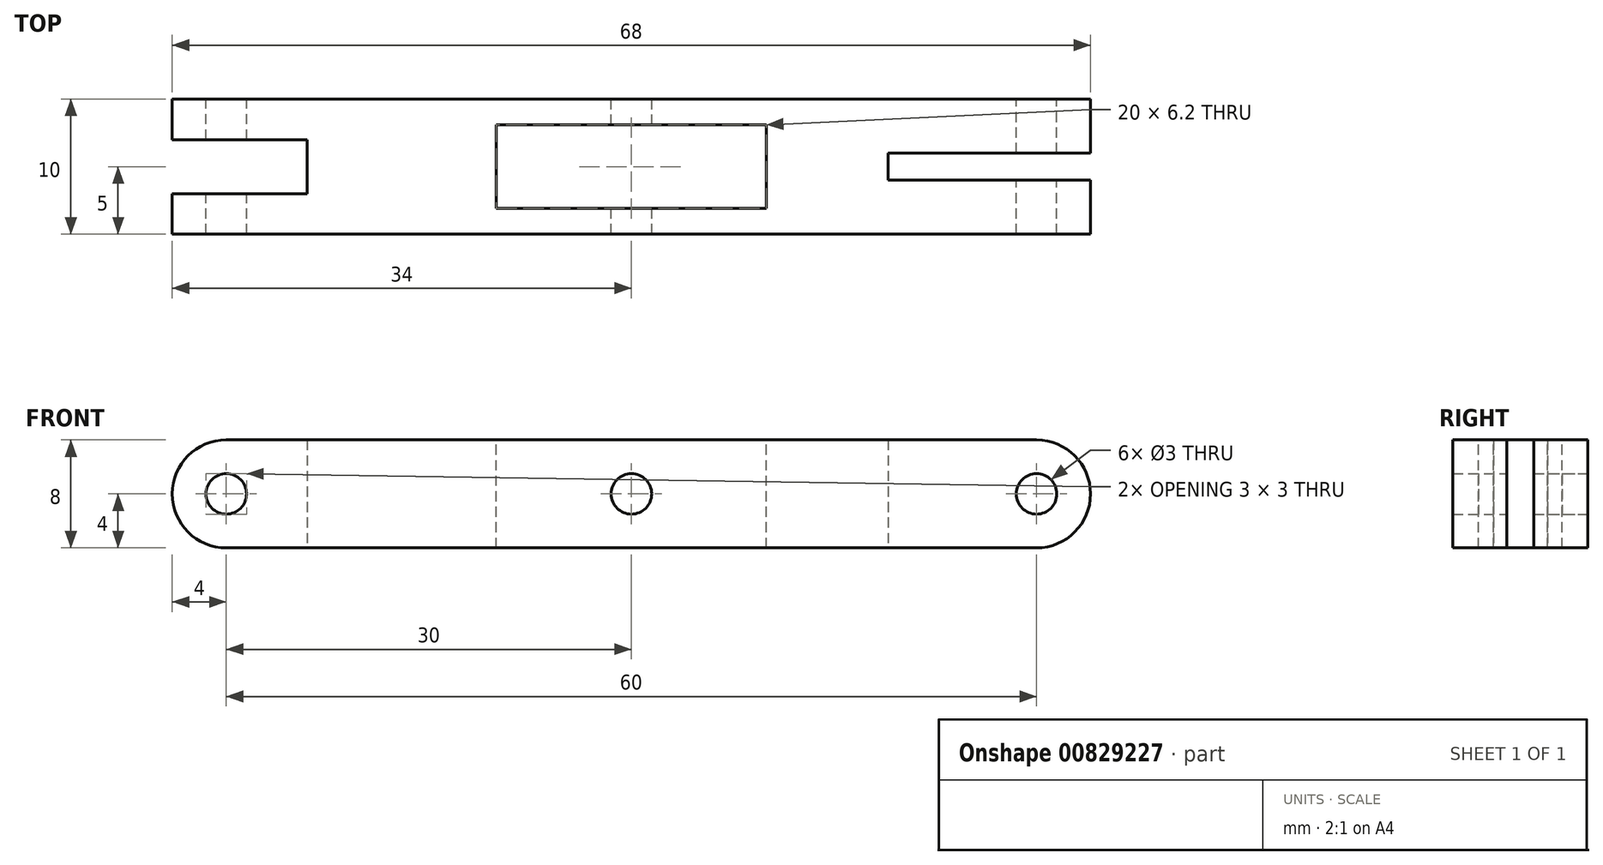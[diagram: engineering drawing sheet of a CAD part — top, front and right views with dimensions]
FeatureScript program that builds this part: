
annotation { "Feature Type Name" : "Feature", "Feature Type Description" : "" }
export const myFeature = defineFeature(function(context is Context, id is Id, definition is map)
    precondition{}
    {
        {
            var Q0;
            Q0=qCreatedBy(makeId("Front.planeOp"),FACE);
            var sketch = newSketch(context, id + "F0", { "sketchPlane" : qUnion([Q0])});
            skLineSegment(sketch, "E0.bottom", {"start": v(30, 4) * mm, "end": v(-30, 4) * mm});
            skLineSegment(sketch, "E0.top", {"start": v(30, -4) * mm, "end": v(-30, -4) * mm});
            skPoint(sketch, "E0.middle", {"position": v(0, 0) * mm});
            skArc(sketch, "E1", {"start": v(-30, 4) * mm, "mid": v(-34, 0) * mm, "end": v(-30, -4) * mm});
            skArc(sketch, "E2", {"start": v(30, -4) * mm, "mid": v(34, 0) * mm, "end": v(30, 4) * mm});
            skCircle(sketch, "E3", {"center": v(-30, 0) * mm, "radius": 1.5 * mm});
            skCircle(sketch, "E4", {"center": v(0, 0) * mm, "radius": 1.5 * mm});
            skCircle(sketch, "E5", {"center": v(30, 0) * mm, "radius": 1.5 * mm});
            skSolve(sketch);
        }
        {
            var Q0;
            Q0 = qSketchRegion(id + "F0", true);
            extrude(context, id + "F1", {"entities" : qUnion([Q0]), "endBound" : BoundingType.SYMMETRIC, "depth" : 10 * mm, "offsetDistance" : 25 * mm});
        }
        {
            var Q0;
            Q0=qCreatedBy(makeId("Right.planeOp"),FACE);
            cPlane(context, id + "F2", {"entities" : qUnion([Q0]), "cplaneType" : CPlaneType.OFFSET, "offset" : 64 * mm, "width" : 150 * mm, "height" : 150 * mm});
        }
        {
            var Q0;
            Q0=qCreatedBy(id+"F2.planeOp",FACE);
            var sketch = newSketch(context, id + "F3", { "sketchPlane" : qUnion([Q0])});
            skLineSegment(sketch, "E6.bottom", {"start": v(1, 4) * mm, "end": v(-1, 4) * mm});
            skLineSegment(sketch, "E6.top", {"start": v(1, -4) * mm, "end": v(-1, -4) * mm});
            skLineSegment(sketch, "E6.left", {"start": v(1, 4) * mm, "end": v(1, -4) * mm});
            skLineSegment(sketch, "E6.right", {"start": v(-1, 4) * mm, "end": v(-1, -4) * mm});
            skPoint(sketch, "E6.middle", {"position": v(0, 0) * mm});
            skSolve(sketch);
        }
        {
            var Q0;
            Q0=makeQuery(id+"F3.imprint","IMPRINT",FACE,{"disambiguationData":[TD([[makeQuery(id+"F3.imprint","IMPRINT",EDGE,{"derivedFrom":sQuery(id+"F3.wireOp",EDGE,"E6.bottom")}),1.0]])]});
            extrude(context, id + "F4", {"entities" : qUnion([Q0]), "operationType" : NewBodyOperationType.REMOVE, "oppositeDirection" : true, "depth" : 45 * mm, "offsetDistance" : 25 * mm});
        }
        {
            var Q0;
            Q0=makeQuery(id+"F1.opExtrude","SWEPT_FACE",FACE,{"disambiguationData":[OSD([sQuery(id+"F0.wireOp",EDGE,"E0.bottom")])]});
            var sketch = newSketch(context, id + "F5", { "sketchPlane" : qUnion([Q0])});
            skSolve(sketch);
        }
        {
            var Q0;
            {var subQ2=sQuery(id+"F0.wireOp",EDGE,"E0.bottom");Q0=makeQuery(id+"F5.imprint","IMPRINT",FACE,{"disambiguationData":[TD([[makeQuery(id+"F5.imprint","IMPRINT",EDGE,{"derivedFrom":makeQuery(id+"F1.opExtrude","CAP_EDGE",EDGE,{"disambiguationData":[OSD([subQ2])],"isStart":true})}),1.0]])]});}
            var sketch = newSketch(context, id + "F6", { "sketchPlane" : qUnion([Q0])});
            skLineSegment(sketch, "E7.bottom", {"start": v(10, 3.1) * mm, "end": v(-10, 3.1) * mm});
            skLineSegment(sketch, "E7.top", {"start": v(10, -3.1) * mm, "end": v(-10, -3.1) * mm});
            skLineSegment(sketch, "E7.left", {"start": v(10, 3.1) * mm, "end": v(10, -3.1) * mm});
            skLineSegment(sketch, "E7.right", {"start": v(-10, 3.1) * mm, "end": v(-10, -3.1) * mm});
            skPoint(sketch, "E7.middle", {"position": v(0, 0) * mm});
            skSolve(sketch);
        }
        {
            var Q0;
            Q0 = qSketchRegion(id + "F6", true);
            extrude(context, id + "F7", {"entities" : qUnion([Q0]), "operationType" : NewBodyOperationType.REMOVE, "oppositeDirection" : true, "depth" : 25 * mm, "offsetDistance" : 25 * mm});
        }
        {
            var Q0;
            Q0=qCreatedBy(makeId("Right.planeOp"),FACE);
            cPlane(context, id + "F8", {"entities" : qUnion([Q0]), "cplaneType" : CPlaneType.OFFSET, "offset" : 64 * mm, "oppositeDirection" : true, "width" : 150 * mm, "height" : 150 * mm});
        }
        {
            var Q0;
            Q0=qCreatedBy(id+"F8.planeOp",FACE);
            var sketch = newSketch(context, id + "F9", { "sketchPlane" : qUnion([Q0])});
            skLineSegment(sketch, "E8.bottom", {"start": v(-2, 4) * mm, "end": v(2, 4) * mm});
            skLineSegment(sketch, "E8.top", {"start": v(-2, -4) * mm, "end": v(2, -4) * mm});
            skLineSegment(sketch, "E8.left", {"start": v(-2, 4) * mm, "end": v(-2, -4) * mm});
            skLineSegment(sketch, "E8.right", {"start": v(2, 4) * mm, "end": v(2, -4) * mm});
            skPoint(sketch, "E8.middle", {"position": v(0, 0) * mm});
            skSolve(sketch);
        }
        {
            var Q0;
            Q0 = qSketchRegion(id + "F9", true);
            extrude(context, id + "F10", {"entities" : qUnion([Q0]), "operationType" : NewBodyOperationType.REMOVE, "depth" : 40 * mm, "offsetDistance" : 25 * mm});
        }
    });
